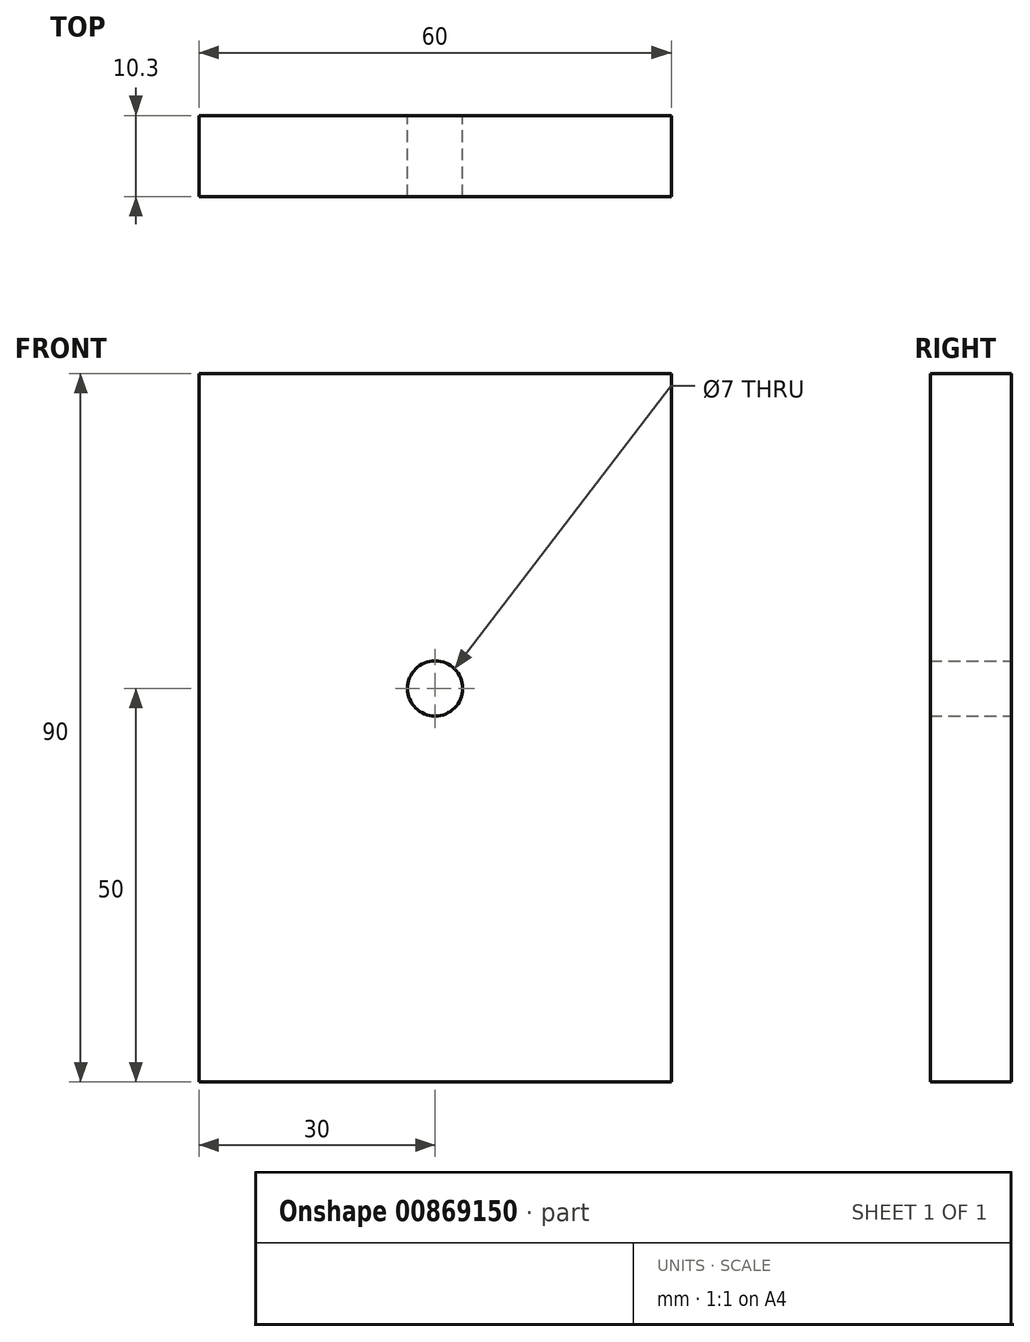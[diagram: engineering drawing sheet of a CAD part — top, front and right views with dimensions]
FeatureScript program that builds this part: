
annotation { "Feature Type Name" : "Feature", "Feature Type Description" : "" }
export const myFeature = defineFeature(function(context is Context, id is Id, definition is map)
    precondition{}
    {
        {
            var Q0;
            Q0=qCreatedBy(makeId("Front.planeOp"),FACE);
            var sketch = newSketch(context, id + "F0", { "sketchPlane" : qUnion([Q0])});
            skLineSegment(sketch, "E0.bottom", {"start": v(-30, 40) * mm, "end": v(30, 40) * mm});
            skLineSegment(sketch, "E0.top", {"start": v(-30, -50) * mm, "end": v(30, -50) * mm});
            skLineSegment(sketch, "E0.left", {"start": v(-30, 40) * mm, "end": v(-30, -50) * mm});
            skLineSegment(sketch, "E0.right", {"start": v(30, 40) * mm, "end": v(30, -50) * mm});
            skPoint(sketch, "E1", {"position": v(-30, 0) * mm});
            skPoint(sketch, "E2", {"position": v(0, 40) * mm});
            skSolve(sketch);
        }
        {
            var Q0;
            Q0=makeQuery(id+"F0.imprint","IMPRINT",FACE,{"disambiguationData":[TD([[makeQuery(id+"F0.imprint","IMPRINT",EDGE,{"derivedFrom":sQuery(id+"F0.wireOp",EDGE,"E0.bottom")}),-1.0]])]});
            var sketch = newSketch(context, id + "F1", { "sketchPlane" : qUnion([Q0])});
            skCircle(sketch, "E3", {"center": v(0, 0) * mm, "radius": 3.5 * mm});
            skSolve(sketch);
        }
        {
            var Q0;
            Q0=qSketchRegion(id+"F0",true);
            extrude(context, id + "F2", {"entities" : qUnion([Q0]), "depth" : 10.3 * mm, "offsetDistance" : 25.4 * mm});
        }
        {
            var Q0;
            Q0=qSketchRegion(id+"F1",true);
            extrude(context, id + "F3", {"entities" : qUnion([Q0]), "operationType" : NewBodyOperationType.REMOVE, "depth" : 25.4 * mm, "offsetDistance" : 25.4 * mm});
        }
    });
